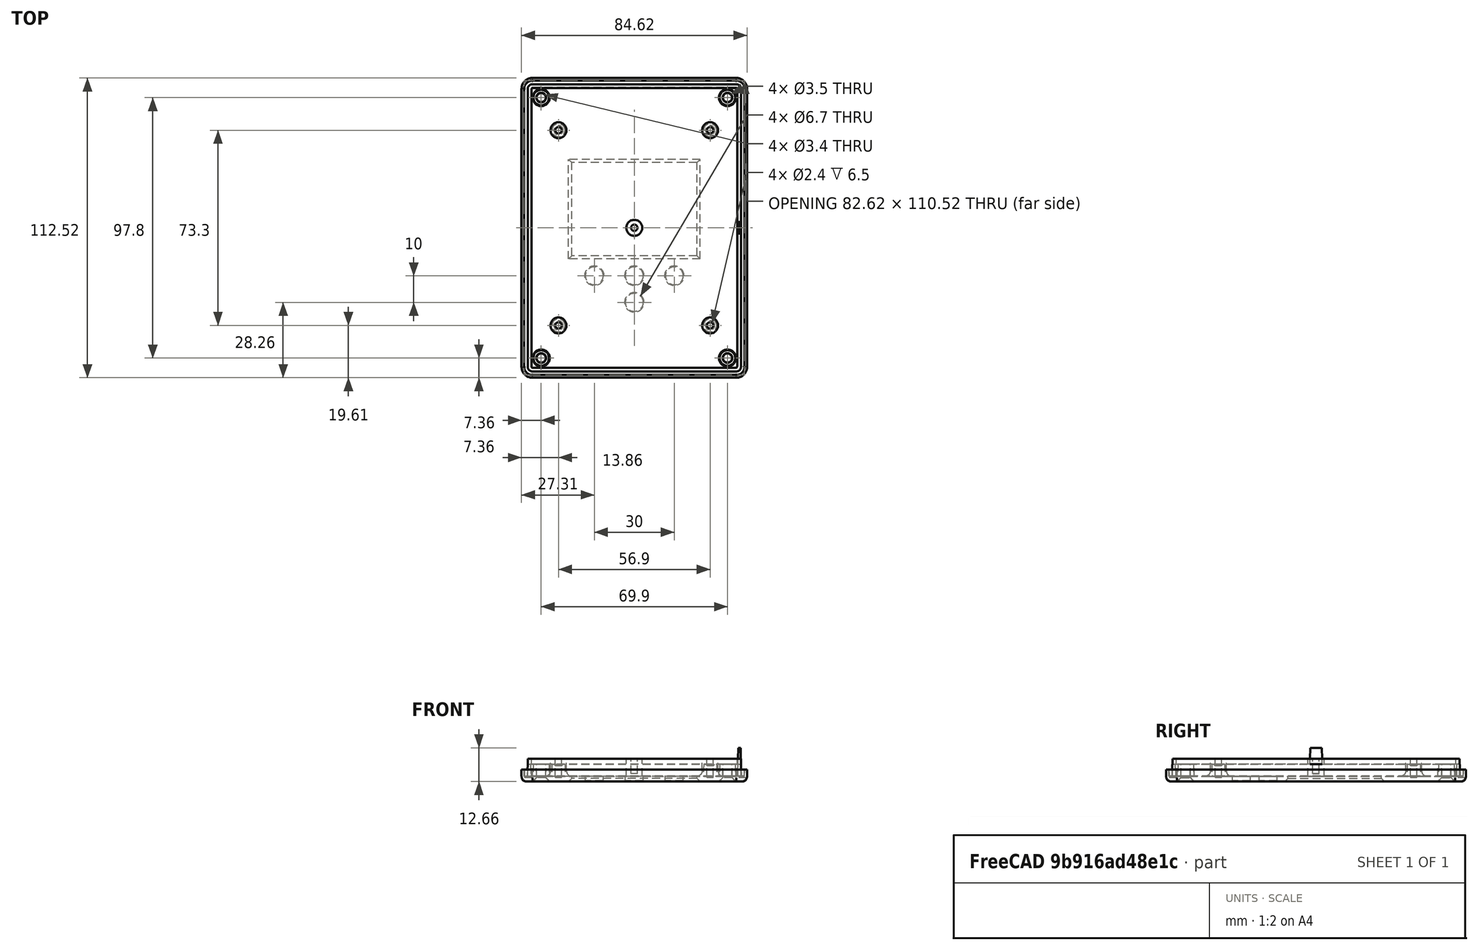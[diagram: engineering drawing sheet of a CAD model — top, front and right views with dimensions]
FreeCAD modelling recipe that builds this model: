
FCSTD DOCUMENT  (FreeCAD 0.18R16110 (Git))
Label: Hammond-front-UPC-v5
License: All rights reserved
LicenseURL: http://en.wikipedia.org/wiki/All_rights_reserved
objects: Part::Cylinder×22, Part::Cut×8, Part::MultiFuse×6, Part::Box×5, Part::Fillet×5, Part::Chamfer×3, Part::Feature×1, App::Part×1
note: 50 computed .brp shape members not serialized (recipe doc carries the construction recipe); baked Part::Feature solids carry a one-line shape summary decoded from their .brp

FEATURE [Part::Feature] Part__Feature001  label="1591XXS2"
  Placement = pos=(0,0,2.55) rot=(1,0,0;3.14159rad)
  shape: bbox 84.64 x 112.5 x 12.62 mm, 136 faces (baked)
FEATURE [App::Part] _591XXS  label="1591XXS"
  Origin = -> Origin
  Placement = pos=(0,0,2.5) rot=(1,0,0;4.71239rad)
FEATURE [Part::Box] Box001  label="-TFT"
  AttacherType = Attacher::AttachEngine3D
  Height = 10
  Length = 47
  Placement = pos=(-23.5,-10.5,-4) rot=(0,0,1;0rad)
  Width = 35
FEATURE [Part::Cylinder] Cylinder003  label="button001"
  Angle = 360
  AttacherType = Attacher::AttachEngine3D
  Height = 10
  Placement = pos=(0,-13,-4) rot=(0,0,1;0rad)
  Radius = 3.35
FEATURE [Part::Cylinder] Cylinder004  label="button002"
  Angle = 360
  AttacherType = Attacher::AttachEngine3D
  Height = 10
  Placement = pos=(-15,-13,-4) rot=(0,0,1;0rad)
  Radius = 3.35
FEATURE [Part::Cylinder] Cylinder005  label="button003"
  Angle = 360
  AttacherType = Attacher::AttachEngine3D
  Height = 10
  Placement = pos=(15,-13,-4) rot=(0,0,1;0rad)
  Radius = 3.35
FEATURE [Part::Cylinder] Cylinder006  label="button004"
  Angle = 360
  AttacherType = Attacher::AttachEngine3D
  Height = 10
  Placement = pos=(0,-23,-4) rot=(0,0,1;0rad)
  Radius = 3.35
FEATURE [Part::Box] Box002  label="Rand buiten"
  AttacherType = Attacher::AttachEngine3D
  Height = 6.5
  Length = 80
  Placement = pos=(-40,-53.9,0) rot=(0,0,1;0rad)
  Width = 107.8
FEATURE [Part::Fillet] Fillet
  Base = -> Box002
  Edges = 4 edges r=1.7: [Edge1,Edge3,Edge5,Edge7]
FEATURE [Part::Box] Box003  label="Rand binnen"
  AttacherType = Attacher::AttachEngine3D
  Height = 10
  Length = 77.2
  Placement = pos=(-38.6,-52.5,0) rot=(0,0,1;0rad)
  Width = 105
FEATURE [Part::Fillet] Fillet001
  Base = -> Box003
  Edges = 4 edges r=0.5: [Edge1,Edge3,Edge5,Edge7]
FEATURE [Part::Cut] Cut003  label="+Rand 1.4 dik"
  Base = -> Fillet
  Tool = -> Fillet001
FEATURE [Part::Box] Box004  label="Front 112,52x84,62"
  AttacherType = Attacher::AttachEngine3D
  Height = 4.5
  Length = 84.62
  Placement = pos=(-42.31,-56.26,-2) rot=(0,0,1;0rad)
  Width = 112.52
FEATURE [Part::Fillet] Fillet002
  Base = -> Box004
  Edges = 4 edges r=4: [Edge1,Edge3,Edge5,Edge7]
FEATURE [Part::Box] Box005  label="binnen"
  AttacherType = Attacher::AttachEngine3D
  Height = 4
  Length = 82.62
  Placement = pos=(-41.31,-55.26,0) rot=(0,0,1;0rad)
  Width = 110.52
FEATURE [Part::Fillet] Fillet003
  Base = -> Box005
  Edges = 4 edges r=3: [Edge1,Edge3,Edge5,Edge7]
FEATURE [Part::Cylinder] Cylinder007  label="Bus front 1 "
  Angle = 360
  AttacherType = Attacher::AttachEngine3D
  Height = 4.5
  Placement = pos=(34.95,48.9,0) rot=(0,0,1;0rad)
  Radius = 3.2
FEATURE [Part::Cylinder] Cylinder008  label="Schroef front 1"
  Angle = 360
  AttacherType = Attacher::AttachEngine3D
  Height = 11.5
  Placement = pos=(34.95,48.9,-4) rot=(0,0,1;0rad)
  Radius = 1.7
FEATURE [Part::Cylinder] Cylinder009  label="Bus front 2 "
  Angle = 360
  AttacherType = Attacher::AttachEngine3D
  Height = 4.5
  Placement = pos=(-34.95,48.9,0) rot=(0,0,1;0rad)
  Radius = 3.2
FEATURE [Part::Cylinder] Cylinder010  label="Bus front 3"
  Angle = 360
  AttacherType = Attacher::AttachEngine3D
  Height = 4.5
  Placement = pos=(-34.95,-48.9,0) rot=(0,0,1;0rad)
  Radius = 3.2
FEATURE [Part::Cylinder] Cylinder011  label="Bus front 4"
  Angle = 360
  AttacherType = Attacher::AttachEngine3D
  Height = 4.5
  Placement = pos=(34.95,-48.9,0) rot=(0,0,1;0rad)
  Radius = 3.2
FEATURE [Part::Cylinder] Cylinder012  label="Schroef front 002"
  Angle = 360
  AttacherType = Attacher::AttachEngine3D
  Height = 11.5
  Placement = pos=(-34.95,48.9,-4) rot=(0,0,1;0rad)
  Radius = 1.7
FEATURE [Part::Cylinder] Cylinder013  label="Schroef front 003"
  Angle = 360
  AttacherType = Attacher::AttachEngine3D
  Height = 11.5
  Placement = pos=(-34.95,-48.9,-4) rot=(0,0,1;0rad)
  Radius = 1.7
FEATURE [Part::Cylinder] Cylinder014  label="Schroef front 004"
  Angle = 360
  AttacherType = Attacher::AttachEngine3D
  Height = 11.5
  Placement = pos=(34.95,-48.9,-4) rot=(0,0,1;0rad)
  Radius = 1.7
FEATURE [Part::MultiFuse] Fusion  label="-Schroeven front"
  Shapes = -> [Cylinder012,Cylinder013,Cylinder014,Cylinder008]
FEATURE [Part::MultiFuse] Fusion002  label="+Bussen front"
  Shapes = -> [Cylinder011,Cylinder007,Cylinder009,Cylinder010]
FEATURE [Part::Cylinder] Cylinder015  label="Schroefgat001"
  Angle = 360
  AttacherType = Attacher::AttachEngine3D
  Height = 5.5
  Placement = pos=(0,0,1) rot=(0,0,1;0rad)
  Radius = 1.2
FEATURE [Part::Cylinder] Cylinder016  label="Bus buiten001"
  Angle = 360
  AttacherType = Attacher::AttachEngine3D
  Height = 6.5
  Radius = 3
FEATURE [Part::Cut] Cut005  label="mal Bus PCB"
  Base = -> Cylinder016
  Tool = -> Cylinder015
FEATURE [Part::MultiFuse] Fusion004  label="-Buttons"
  Placement = pos=(0,-5,0) rot=(0,0,1;0rad)
  Shapes = -> [Cylinder003,Cylinder005,Cylinder006,Cylinder004]
FEATURE [Part::Cut] Cut  label="+Front kaal"
  Base = -> Fillet002
  Tool = -> Fillet003
FEATURE [Part::MultiFuse] Fusion005  label="-"
  Shapes = -> [Fusion,Box001,Fusion004]
FEATURE [Part::Cylinder] Cylinder001  label="Schroefgat"
  Angle = 360
  AttacherType = Attacher::AttachEngine3D
  Height = 6.5
  Radius = 1.2
FEATURE [Part::Cylinder] Cylinder  label="Bus buiten"
  Angle = 360
  AttacherType = Attacher::AttachEngine3D
  Height = 6.5
  Radius = 3
FEATURE [Part::Cut] Cut007  label="Bus 1"
  Base = -> Cylinder
  Placement = pos=(28.45,36.65,0) rot=(0,0,1;0rad)
  Tool = -> Cylinder001
FEATURE [Part::Cylinder] Cylinder017  label="Schroefgat002"
  Angle = 360
  AttacherType = Attacher::AttachEngine3D
  Height = 6.5
  Radius = 1.2
FEATURE [Part::Cylinder] Cylinder018  label="Bus buiten002"
  Angle = 360
  AttacherType = Attacher::AttachEngine3D
  Height = 6.5
  Radius = 3
FEATURE [Part::Cut] Cut008  label="Bus 2"
  Base = -> Cylinder018
  Placement = pos=(-28.45,36.65,0) rot=(0,0,1;0rad)
  Tool = -> Cylinder017
FEATURE [Part::Cylinder] Cylinder019  label="Schroefgat003"
  Angle = 360
  AttacherType = Attacher::AttachEngine3D
  Height = 6.5
  Radius = 1.2
FEATURE [Part::Cylinder] Cylinder020  label="Bus buiten003"
  Angle = 360
  AttacherType = Attacher::AttachEngine3D
  Height = 6.5
  Radius = 3
FEATURE [Part::Cut] Cut009  label="Bus 3"
  Base = -> Cylinder020
  Placement = pos=(-28.45,-36.65,0) rot=(0,0,1;0rad)
  Tool = -> Cylinder019
FEATURE [Part::Cylinder] Cylinder021  label="Schroefgat004"
  Angle = 360
  AttacherType = Attacher::AttachEngine3D
  Height = 6.5
  Radius = 1.2
FEATURE [Part::Cylinder] Cylinder022  label="Bus buiten004"
  Angle = 360
  AttacherType = Attacher::AttachEngine3D
  Height = 6.5
  Radius = 3
FEATURE [Part::Cut] Cut010  label="Bus 4"
  Base = -> Cylinder022
  Placement = pos=(28.45,-36.65,0) rot=(0,0,1;0rad)
  Tool = -> Cylinder021
FEATURE [Part::MultiFuse] Fusion001  label="+Bussen"
  Shapes = -> [Cut007,Cut008,Cut009,Cut010]
FEATURE [Part::MultiFuse] Fusion006  label="+"
  Shapes = -> [Cut003,Fusion002,Fusion001,Cut]
FEATURE [Part::Cut] Cut006
  Base = -> Fusion006
  Tool = -> Fusion005
FEATURE [Part::Chamfer] Chamfer  label="front taps M3"
  Base = -> Cut006
  Edges = 4 edges r=1.55: [Edge29,Edge34,Edge39,Edge40]
FEATURE [Part::Fillet] Fillet004  label="FDM fillet bussen en rand"
  Base = -> Chamfer
  Edges = 5 edges r=2: [Edge6,Edge79,Edge81,Edge82,Edge83]
FEATURE [Part::Chamfer] Chamfer001  label="SLS chamfer front"
  Base = -> Fillet004
  Edges = 4 edges r=1.2: [Edge14,Edge15,Edge16,Edge17]
FEATURE [Part::Chamfer] Chamfer002  label="Chamfer buttons"
  Base = -> Chamfer001
  Edges = 4 edges r=0.3: [Edge14,Edge15,Edge16,Edge17]
